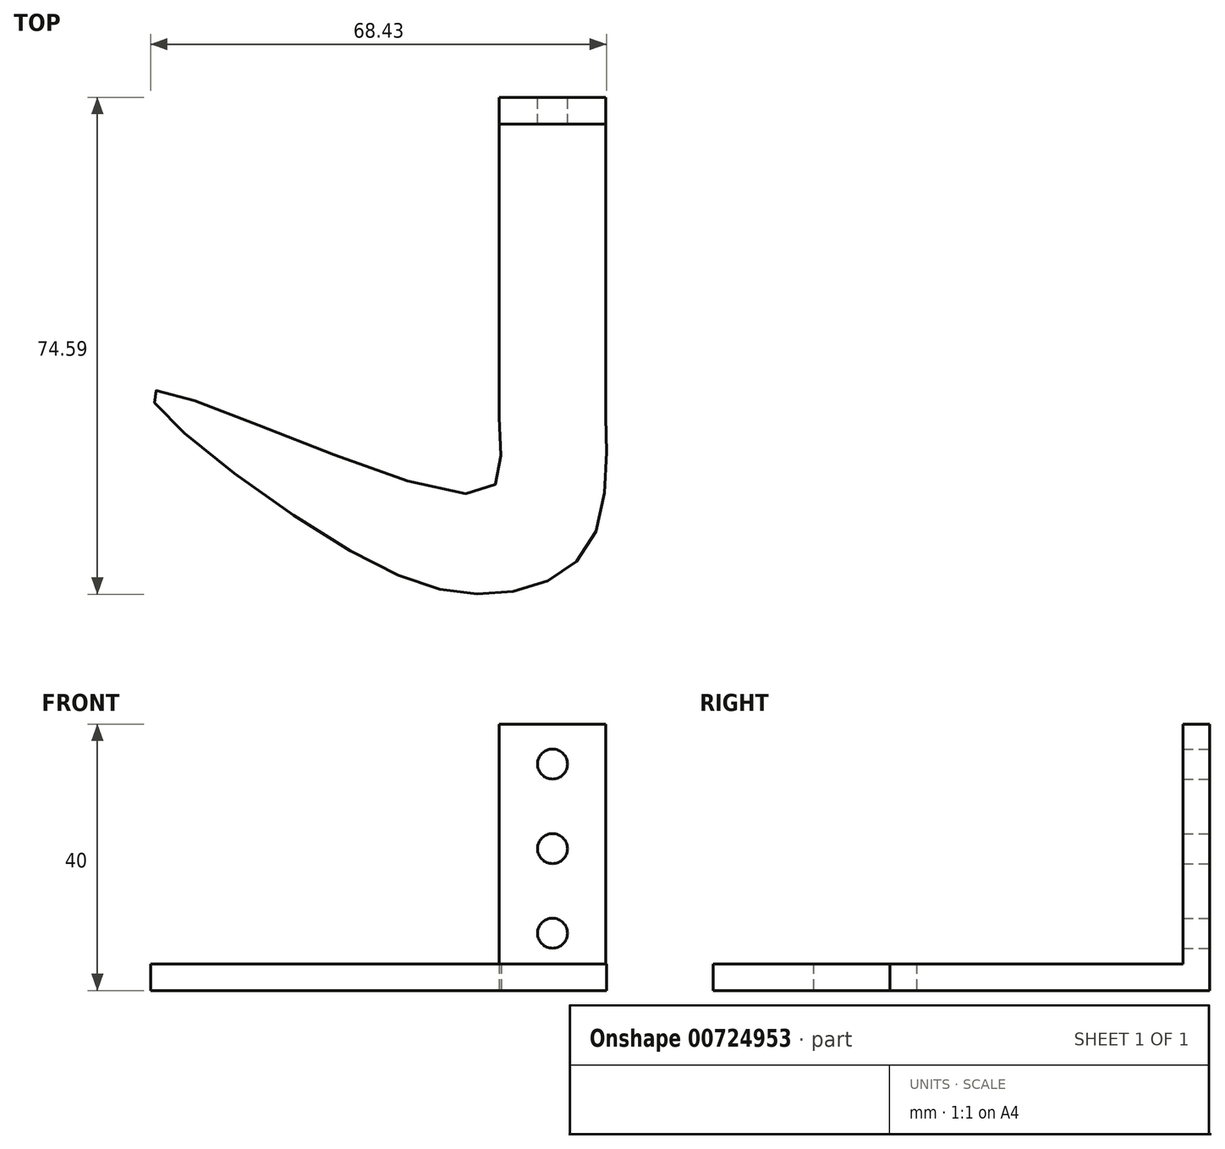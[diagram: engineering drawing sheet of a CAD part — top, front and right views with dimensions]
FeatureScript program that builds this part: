
annotation { "Feature Type Name" : "Feature", "Feature Type Description" : "" }
export const myFeature = defineFeature(function(context is Context, id is Id, definition is map)
    precondition{}
    {
        {
            var Q0;
            Q0=qCreatedBy(makeId("Top.planeOp"),FACE);
            var sketch = newSketch(context, id + "F0", { "sketchPlane" : qUnion([Q0])});
            skLineSegment(sketch, "E0", {"start": v(0, 0) * mm, "end": v(16, 0) * mm});
            skLineSegment(sketch, "E1", {"start": v(16, -48) * mm, "end": v(16, 0) * mm});
            skLineSegment(sketch, "E2", {"start": v(0, 0) * mm, "end": v(0, -48) * mm});
            skFitSpline(sketch, "E3", {"points": [v(0, -48) * mm, v(-2.86, -59.4) * mm, v(-51.89, -44.07) * mm, v(-24.82, -66.62) * mm, v(0, -74.45) * mm, v(13.69, -66.93) * mm, v(16, -48) * mm], "startDerivative": vector(0, -139.45) * mm, "endDerivative": vector(-1.9, 105.29) * mm});
            skSolve(sketch);
        }
        {
            var Q0;
            Q0=makeQuery(id+"F0.imprint","IMPRINT",FACE,{"disambiguationData":[TD([[makeQuery(id+"F0.imprint","IMPRINT",EDGE,{"derivedFrom":sQuery(id+"F0.wireOp",EDGE,"E0")}),-1.0]])]});
            extrude(context, id + "F1", {"entities" : qUnion([Q0]), "depth" : 4 * mm, "offsetDistance" : 25 * mm});
        }
        {
            var Q0;
            Q0=makeQuery(id+"F1.opExtrude","CAP_FACE",FACE,{"disambiguationData":[OSD([sQuery(id+"F0.wireOp",EDGE,"E0"),sQuery(id+"F0.wireOp",EDGE,"E1"),sQuery(id+"F0.wireOp",EDGE,"E2"),sQuery(id+"F0.wireOp",EDGE,"E3")])],"isStart":false});
            var sketch = newSketch(context, id + "F2", { "sketchPlane" : qUnion([Q0])});
            skLineSegment(sketch, "E4", {"start": v(0, 0) * mm, "end": v(16, 0) * mm});
            skLineSegment(sketch, "E5", {"start": v(16, 0) * mm, "end": v(16, -4) * mm});
            skLineSegment(sketch, "E6", {"start": v(16, -4) * mm, "end": v(0, -4) * mm});
            skLineSegment(sketch, "E7", {"start": v(0, -4) * mm, "end": v(0, 0) * mm});
            skSolve(sketch);
        }
        {
            var Q0;
            Q0=makeQuery(id+"F2.imprint","IMPRINT",FACE,{"disambiguationData":[TD([[makeQuery(id+"F2.imprint","IMPRINT",EDGE,{"derivedFrom":sQuery(id+"F2.wireOp",EDGE,"E4")}),-1.0]])]});
            extrude(context, id + "F3", {"entities" : qUnion([Q0]), "operationType" : NewBodyOperationType.ADD, "depth" : 36 * mm, "offsetDistance" : 25 * mm});
        }
        {
            var Q0;
            Q0=makeQuery(id+"F3.boolean.opBoolean","MERGE",FACE,{"derivedFrom":[makeQuery(id+"F1.opExtrude","SWEPT_FACE",FACE,{"disambiguationData":[OSD([sQuery(id+"F0.wireOp",EDGE,"E0")])]}),makeQuery(id+"F3.opExtrude","SWEPT_FACE",FACE,{"disambiguationData":[OSD([sQuery(id+"F2.wireOp",EDGE,"E4")])]})]});
            var sketch = newSketch(context, id + "F4", { "sketchPlane" : qUnion([Q0])});
            skPoint(sketch, "E8", {"position": v(-8, 34) * mm});
            skPoint(sketch, "E9", {"position": v(-8, 21.3) * mm});
            skPoint(sketch, "E10", {"position": v(-8, 8.6) * mm});
            skPoint(sketch, "E11", {"position": v(25.87, 49.94) * mm});
            skSolve(sketch);
        }
        {
            var Q0;
            Q0=sQuery(id+"F4.wireOp",VERTEX,"E9");
            var Q1;
            Q1=sQuery(id+"F4.wireOp",VERTEX,"E10");
            var Q2;
            Q2=sQuery(id+"F4.wireOp",VERTEX,"E8");
            var Q3;
            Q3=makeQuery(id+"F1.opExtrude","SWEPT_BODY",BODY,{"disambiguationData":[OSD([sQuery(id+"F0.wireOp",EDGE,"E0"),sQuery(id+"F0.wireOp",EDGE,"E1"),sQuery(id+"F0.wireOp",EDGE,"E2"),sQuery(id+"F0.wireOp",EDGE,"E3")])]});
            hole(context, id + "F5", {"style" : HoleStyle.SIMPLE, "endStyle" : HoleEndStyle.THROUGH, "standardTappedOrClearance" : lookupTablePath({ "standard" : "ANSI", "fit" : "Normal (ASME)", "size" : "#8", "type" : "Clearance" }), "standardBlindInLast" : lookupTablePath({ "fit" : "Free", "standard" : "ANSI", "size" : "#8", "type" : "Clearance" }), "holeDiameter" : 4.5 * mm, "majorDiameter" : 5 * mm, "isTappedThrough" : true, "tappedDepth" : 12 * mm, "tapClearance" : 3, "locations" : qUnion([Q0, Q1, Q2]), "scope" : qUnion([Q3])});
        }
    });
